# Revit family: DCS_Revit_18_SBE1-142-N_or_L_Side_Burner_90000777A
name_source: partatom
category: Specialty Equipment
revit_build: Autodesk Revit 2018 (Build: 20170223_1515(x64)
units: mm (PartAtom-declared; Revit-internal decimal feet)

## family parameters
Always vertical = Yes
Cut with Voids When Loaded = Yes
OmniClass Number = 23.40.40.14.17.27
OmniClass Title = Barbecues
Part Type = Normal
Room Calculation Point = No
Round Connector Dimension = Use Diameter
Shared = No
Work Plane-Based = No

## types (2) — shared parameters
Cavity - Depth = 578 mm  [stored 1.89633 ft]
Cavity - Height = 257 mm  [stored 0.843176 ft]
Cavity - Width = 308 mm  [stored 1.0105 ft]
Chassis - Depth = 576 mm  [stored 1.88976 ft]
Chassis - Height = 253 mm  [stored 0.830052 ft]
Chassis - Width = 301 mm  [stored 0.987533 ft]
Clearance - Below Combustible = 305 mm  [stored 1.00066 ft]
Clearance - Rear Combustible = 152 mm  [stored 0.498688 ft]
Clearance - Rear Non-Combustible = 76 mm  [stored 0.249344 ft]
Clearance - Side Combustible = 152 mm  [stored 0.498688 ft]
Clearance - Side Non-Combustible = 76 mm  [stored 0.249344 ft]
Connector Description - Electrical = 120 V, 15 A, GFI electrical outlet
Description = Double Side Burner
Manufacturer = Fisher & Paykel
Material - Body = DCS - Stainless Steel
Model = SBE1-142-N or SBE1-142-L
Product - Depth = 693 mm  [stored 2.27362 ft]
Product - Height = 310 mm  [stored 1.01706 ft]
Product - Width = 373 mm  [stored 1.22375 ft]
URL = www.dcsappliances.com
Visibility - Clearance Required = Yes
Visibility - Clearance Required (Below Countertop) = Yes

## per-type parameters (varying)
| type | Connector Description - Gas | Visibility - Cover |
| Double Side Burner | Operating Pressure NG 4” WC, LPG 11” WC, Connection is 1/2” NPT Coupling | Yes |
| Double Side Burner (without covers) | Operating Pressure NG 4” WC, LPG 11” WC, Connection is 1/2” NPT female | No |

note: [stored X ft] marks values corroborated as IEEE doubles in the binary element streams (Revit-internal decimal feet)

## geometry (parser evidence)
native form markers: Sweep x14
no freeform markers — native parametric forms only
